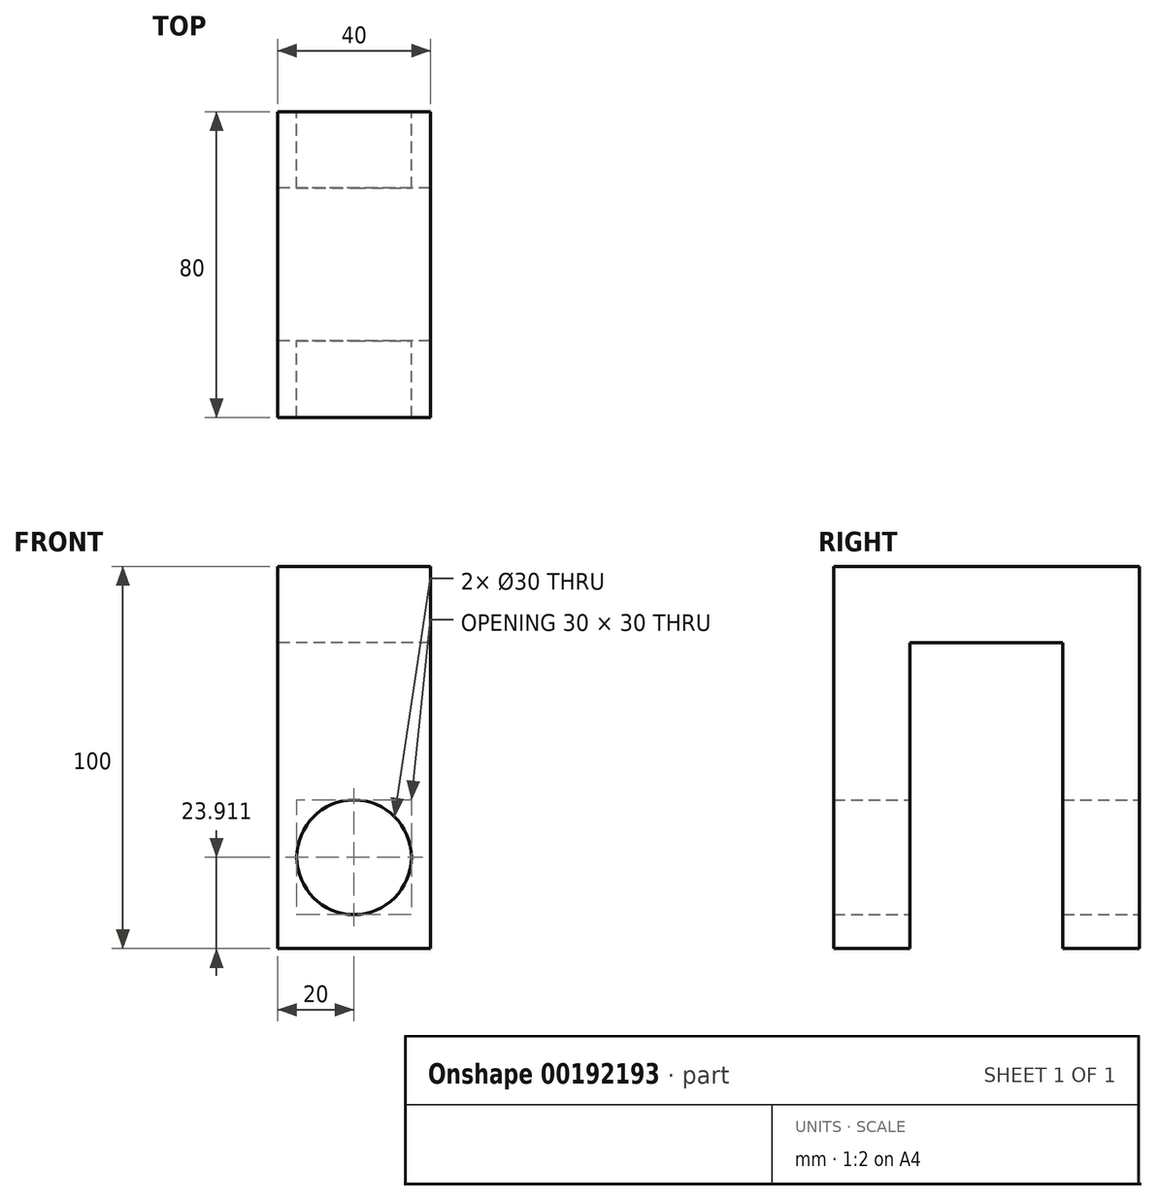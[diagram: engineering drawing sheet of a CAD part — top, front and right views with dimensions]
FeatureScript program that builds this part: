
annotation { "Feature Type Name" : "Feature", "Feature Type Description" : "" }
export const myFeature = defineFeature(function(context is Context, id is Id, definition is map)
    precondition{}
    {
        {
            var Q0;
            Q0=qCreatedBy(makeId("Front.planeOp"),FACE);
            var sketch = newSketch(context, id + "F0", { "sketchPlane" : qUnion([Q0])});
            skLineSegment(sketch, "E0.bottom", {"start": v(-20, -50) * mm, "end": v(20, -50) * mm});
            skLineSegment(sketch, "E0.top", {"start": v(-20, 50) * mm, "end": v(20, 50) * mm});
            skLineSegment(sketch, "E0.left", {"start": v(-20, -50) * mm, "end": v(-20, 50) * mm});
            skLineSegment(sketch, "E0.right", {"start": v(20, -50) * mm, "end": v(20, 50) * mm});
            skPoint(sketch, "E0.middle", {"position": v(0, 0) * mm});
            skCircle(sketch, "E1", {"center": v(0, -26.09) * mm, "radius": 15 * mm});
            skSolve(sketch);
        }
        {
            var Q0;
            Q0 = qSketchRegion(id + "F0", true);
            extrude(context, id + "F1", {"entities" : qUnion([Q0]), "depth" : 80 * mm, "symmetric" : true});
        }
        {
            var Q0;
            Q0=makeQuery(id+"F1.opExtrude","SWEPT_FACE",FACE,{"disambiguationData":[OSD([sQuery(id+"F0.wireOp",EDGE,"E0.left")])]});
            var sketch = newSketch(context, id + "F2", { "sketchPlane" : qUnion([Q0])});
            skLineSegment(sketch, "E2.bottom", {"start": v(-20, 30) * mm, "end": v(20, 30) * mm});
            skLineSegment(sketch, "E2.top", {"start": v(-20, -130) * mm, "end": v(20, -130) * mm});
            skLineSegment(sketch, "E2.left", {"start": v(-20, 30) * mm, "end": v(-20, -130) * mm});
            skLineSegment(sketch, "E2.right", {"start": v(20, 30) * mm, "end": v(20, -130) * mm});
            skPoint(sketch, "E2.middle", {"position": v(0, -50) * mm});
            skSolve(sketch);
        }
        {
            var Q0;
            {var subQ0=sQuery(id+"F2.wireOp",EDGE,"E2.bottom");Q0=makeQuery(id+"F2.imprint","IMPRINT",FACE,{"disambiguationData":[TD([[makeQuery(id+"F2.imprint","IMPRINT",EDGE,{"derivedFrom":subQ0}),-1.0]])]});}
            extrude(context, id + "F3", {"entities" : qUnion([Q0]), "operationType" : NewBodyOperationType.REMOVE, "oppositeDirection" : true, "depth" : 120 * mm, "symmetric" : true});
        }
    });
